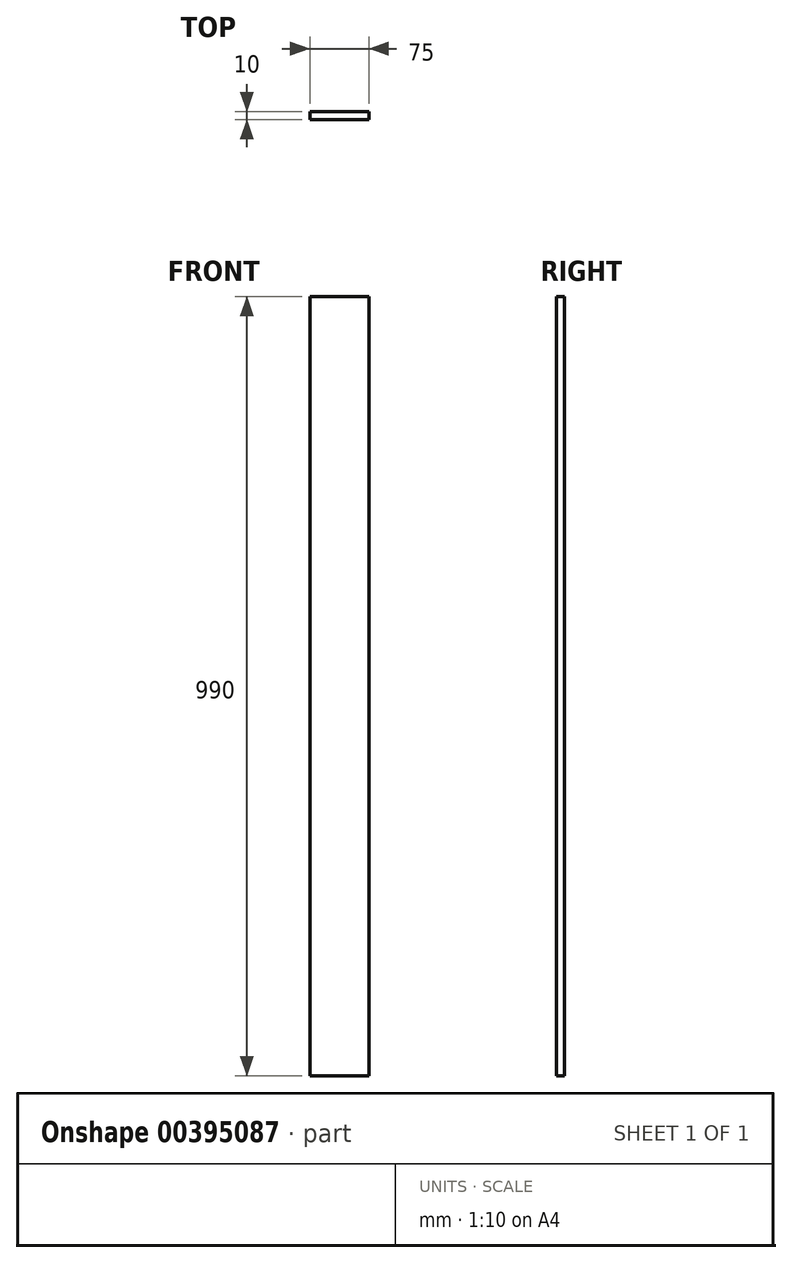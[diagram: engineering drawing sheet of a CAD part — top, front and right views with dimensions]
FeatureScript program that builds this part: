
annotation { "Feature Type Name" : "Feature", "Feature Type Description" : "" }
export const myFeature = defineFeature(function(context is Context, id is Id, definition is map)
    precondition{}
    {
        {
            var Q0;
            Q0=qCreatedBy(makeId("Front.planeOp"),FACE);
            var sketch = newSketch(context, id + "F0", { "sketchPlane" : qUnion([Q0])});
            skLineSegment(sketch, "E0.bottom", {"start": v(-37.5, -495) * mm, "end": v(37.5, -495) * mm});
            skLineSegment(sketch, "E0.top", {"start": v(-37.5, 495) * mm, "end": v(37.5, 495) * mm});
            skLineSegment(sketch, "E0.left", {"start": v(-37.5, -495) * mm, "end": v(-37.5, 495) * mm});
            skLineSegment(sketch, "E0.right", {"start": v(37.5, -495) * mm, "end": v(37.5, 495) * mm});
            skPoint(sketch, "E0.middle", {"position": v(0, 0) * mm});
            skSolve(sketch);
        }
        {
            var Q0;
            Q0 = qSketchRegion(id + "F0", true);
            extrude(context, id + "F1", {"entities" : qUnion([Q0]), "depth" : 10 * mm});
        }
    });
